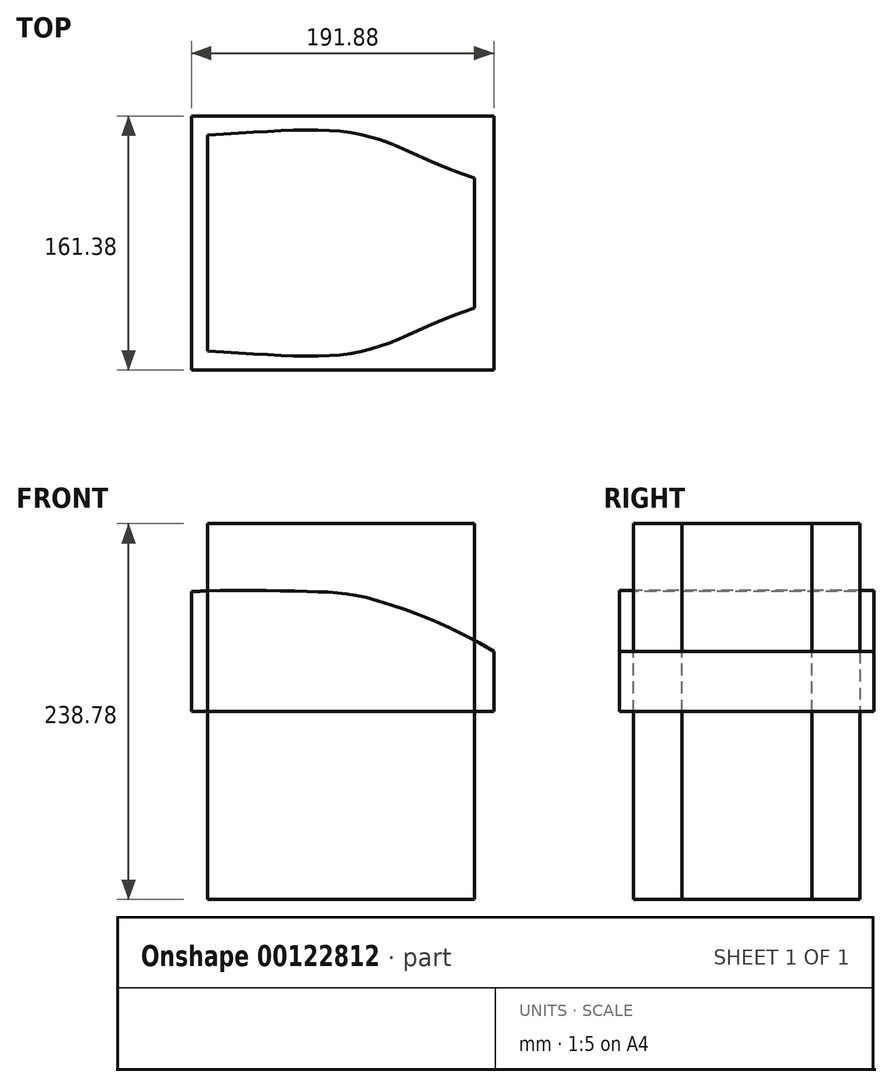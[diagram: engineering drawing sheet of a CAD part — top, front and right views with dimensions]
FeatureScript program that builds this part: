
annotation { "Feature Type Name" : "Feature", "Feature Type Description" : "" }
export const myFeature = defineFeature(function(context is Context, id is Id, definition is map)
    precondition{}
    {
        {
            var Q0;
            Q0=qCreatedBy(makeId("Front.planeOp"),FACE);
            var sketch = newSketch(context, id + "F0", { "sketchPlane" : qUnion([Q0])});
            skLineSegment(sketch, "E0", {"start": v(-99.09, 0) * mm, "end": v(-99.09, 76.2) * mm});
            skLineSegment(sketch, "E1", {"start": v(92.79, 0) * mm, "end": v(92.79, 38.1) * mm});
            skFitSpline(sketch, "E2", {"points": [v(-99.09, 76.2) * mm, v(-23.42, 76.2) * mm, v(12.37, 72.24) * mm, v(92.79, 38.1) * mm], "startDerivative": vector(197.3, 9.66) * mm, "endDerivative": vector(200.1, -125.85) * mm});
            skLineSegment(sketch, "E3", {"start": v(-99.09, 0) * mm, "end": v(92.79, 0) * mm});
            skSolve(sketch);
        }
        {
            var Q0;
            Q0=makeQuery(id+"F0.imprint","IMPRINT",FACE,{"disambiguationData":[TD([[makeQuery(id+"F0.imprint","IMPRINT",EDGE,{"derivedFrom":sQuery(id+"F0.wireOp",EDGE,"E0")}),-1.0]])]});
            var Q1;
            Q1=sQuery(id+"F0.wireOp",EDGE,"E1");
            var Q2;
            Q2=sQuery(id+"F0.wireOp",EDGE,"E2");
            var Q3;
            Q3=sQuery(id+"F0.wireOp",EDGE,"E0");
            var Q4;
            Q4=sQuery(id+"F0.wireOp",EDGE,"E3");
            extrude(context, id + "F1", {"entities" : qUnion([Q0]), "bodyType" : ToolBodyType.SURFACE, "surfaceEntities" : qUnion([Q1, Q2, Q3, Q4]), "endBound" : BoundingType.SYMMETRIC, "depth" : 161.38 * mm});
        }
        {
            var Q0;
            Q0=qCreatedBy(makeId("Top.planeOp"),FACE);
            var sketch = newSketch(context, id + "F2", { "sketchPlane" : qUnion([Q0])});
            skLineSegment(sketch, "E4", {"start": v(-142.12, 0) * mm, "end": v(135.66, 0) * mm, "construction": true});
            skLineSegment(sketch, "E5", {"start": v(-88.95, 0) * mm, "end": v(-88.95, 68.58) * mm});
            skLineSegment(sketch, "E6", {"start": v(80.5, 0) * mm, "end": v(80.5, 41.25) * mm});
            skFitSpline(sketch, "E7", {"points": [v(-88.95, 68.58) * mm, v(10.19, 68.58) * mm, v(80.5, 41.25) * mm], "startDerivative": vector(237.25, 13.22) * mm, "endDerivative": vector(194.35, -62.21) * mm});
            skLineSegment(sketch, "E8.MirrorCS", {"start": v(-88.95, 0) * mm, "end": v(-88.95, -68.58) * mm});
            skLineSegment(sketch, "E9.MirrorCS", {"start": v(80.5, 0) * mm, "end": v(80.5, -41.25) * mm});
            skFitSpline(sketch, "E10.MirrorCS", {"points": [v(-88.95, -68.58) * mm, v(10.19, -68.58) * mm, v(80.5, -41.25) * mm], "startDerivative": vector(237.25, -13.22) * mm, "endDerivative": vector(194.35, 62.21) * mm});
            skSolve(sketch);
        }
        {
            var Q0;
            Q0=makeQuery(id+"F2.imprint","IMPRINT",FACE,{"disambiguationData":[TD([[makeQuery(id+"F2.imprint","IMPRINT",EDGE,{"derivedFrom":sQuery(id+"F2.wireOp",EDGE,"E5")}),-1.0]])]});
            var Q1;
            Q1=sQuery(id+"F2.wireOp",EDGE,"E7");
            var Q2;
            Q2=sQuery(id+"F2.wireOp",EDGE,"E8.MirrorCS");
            var Q3;
            Q3=sQuery(id+"F2.wireOp",EDGE,"E9.MirrorCS");
            var Q4;
            Q4=sQuery(id+"F2.wireOp",EDGE,"E6");
            var Q5;
            Q5=sQuery(id+"F2.wireOp",EDGE,"E5");
            var Q6;
            Q6=sQuery(id+"F2.wireOp",EDGE,"E10.MirrorCS");
            extrude(context, id + "F3", {"entities" : qUnion([Q0]), "bodyType" : ToolBodyType.SURFACE, "surfaceEntities" : qUnion([Q1, Q2, Q3, Q4, Q5, Q6]), "endBound" : BoundingType.SYMMETRIC, "depth" : 238.77 * mm});
        }
    });
